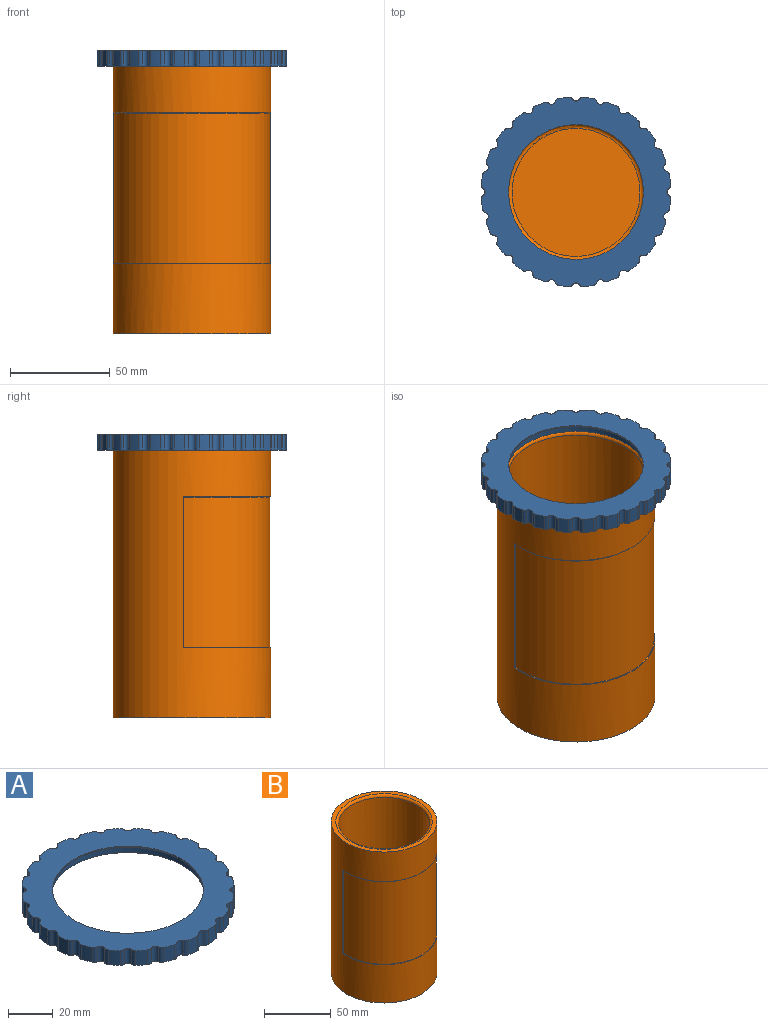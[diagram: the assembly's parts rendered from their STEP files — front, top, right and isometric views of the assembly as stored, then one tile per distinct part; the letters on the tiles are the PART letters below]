
ASSEMBLY  parts=2 mates=1
PART A: 103 faces, bbox 94.7x94.7x8 mm
  f0: cylinder r=34.5mm len=69mm, axis (0,0,-1), area 737mm2, adj f100,f102
  f1: cylinder r=47.5mm len=8mm, axis (0,0,-1), area 42.8mm2, adj f25,f26,f29,f97
  f2: cylinder r=47.5mm len=8mm, axis (0,0,-1), area 42.8mm2, adj f25,f26,f94,f98
  f3: cylinder r=47.5mm len=8mm, axis (0,0,-1), area 42.8mm2, adj f25,f26,f91,f95
  f4: cylinder r=47.5mm len=8mm, axis (0,0,-1), area 42.8mm2, adj f25,f26,f88,f92
  f5: cylinder r=47.5mm len=8mm, axis (0,0,-1), area 42.8mm2, adj f25,f26,f85,f89
  f6: cylinder r=47.5mm len=8mm, axis (0,0,-1), area 42.8mm2, adj f25,f26,f82,f86
  f7: cylinder r=47.5mm len=8mm, axis (0,0,-1), area 42.8mm2, adj f25,f26,f79,f83
  f8: cylinder r=47.5mm len=8mm, axis (0,0,-1), area 42.8mm2, adj f25,f26,f76,f80
  f9: cylinder r=47.5mm len=8mm, axis (0,0,-1), area 42.8mm2, adj f25,f26,f73,f77
  f10: cylinder r=47.5mm len=8mm, axis (0,0,-1), area 42.8mm2, adj f25,f26,f70,f74
  f11: cylinder r=47.5mm len=8mm, axis (0,0,-1), area 42.8mm2, adj f25,f26,f67,f71
  f12: cylinder r=47.5mm len=8mm, axis (0,0,-1), area 42.8mm2, adj f25,f26,f64,f68
  f13: cylinder r=47.5mm len=8mm, axis (0,0,-1), area 42.8mm2, adj f25,f26,f61,f65
  f14: cylinder r=47.5mm len=8mm, axis (0,0,-1), area 42.8mm2, adj f25,f26,f58,f62
  f15: cylinder r=47.5mm len=8mm, axis (0,0,-1), area 42.8mm2, adj f25,f26,f55,f59
  f16: cylinder r=47.5mm len=8mm, axis (0,0,-1), area 42.8mm2, adj f25,f26,f52,f56
  f17: cylinder r=47.5mm len=8mm, axis (0,0,-1), area 42.8mm2, adj f25,f26,f49,f53
  f18: cylinder r=47.5mm len=8mm, axis (0,0,-1), area 42.8mm2, adj f25,f26,f46,f50
  f19: cylinder r=47.5mm len=8mm, axis (0,0,-1), area 42.8mm2, adj f25,f26,f43,f47
  f20: cylinder r=47.5mm len=8mm, axis (0,0,-1), area 42.8mm2, adj f25,f26,f40,f44
  f21: cylinder r=47.5mm len=8mm, axis (0,0,-1), area 42.8mm2, adj f25,f26,f37,f41
  f22: cylinder r=47.5mm len=8mm, axis (0,0,-1), area 42.8mm2, adj f25,f26,f34,f38
  f23: cylinder r=47.5mm len=8mm, axis (0,0,-1), area 42.8mm2, adj f25,f26,f31,f35
  f24: cylinder r=47.5mm len=8mm, axis (0,0,-1), area 42.8mm2, adj f25,f26,f28,f32
  f25: plane 94.75x94.75mm, normal (0,0,1), area 3354mm2, adj f1,f2,f3,f4,f5,f6,f7,f8
  f26: plane 94.75x94.75mm, normal (0,0,-1), area 1895.3mm2, adj f1,f2,f3,f4,f5,f6,f7,f8
  f27: cylinder r=2mm len=8mm, axis (0,0,1), area 32.3mm2, adj f25,f26,f28,f29
  f28: cylinder r=2mm len=8mm, axis (0,0,-1), area 17.4mm2, adj f24,f25,f26,f27
  f29: cylinder r=2mm len=8mm, axis (0,0,-1), area 17.4mm2, adj f1,f25,f26,f27
  f30: cylinder r=2mm len=8mm, axis (0,0,1), area 32.3mm2, adj f25,f26,f31,f32
  f31: cylinder r=2mm len=8mm, axis (0,0,-1), area 17.4mm2, adj f23,f25,f26,f30
  f32: cylinder r=2mm len=8mm, axis (0,0,-1), area 17.4mm2, adj f24,f25,f26,f30
  f33: cylinder r=2mm len=8mm, axis (0,0,1), area 32.3mm2, adj f25,f26,f34,f35
  f34: cylinder r=2mm len=8mm, axis (0,0,-1), area 17.4mm2, adj f22,f25,f26,f33
  f35: cylinder r=2mm len=8mm, axis (0,0,-1), area 17.4mm2, adj f23,f25,f26,f33
  f36: cylinder r=2mm len=8mm, axis (0,0,1), area 32.3mm2, adj f25,f26,f37,f38
  f37: cylinder r=2mm len=8mm, axis (0,0,-1), area 17.4mm2, adj f21,f25,f26,f36
  f38: cylinder r=2mm len=8mm, axis (0,0,-1), area 17.4mm2, adj f22,f25,f26,f36
  f39: cylinder r=2mm len=8mm, axis (0,0,1), area 32.3mm2, adj f25,f26,f40,f41
  f40: cylinder r=2mm len=8mm, axis (0,0,-1), area 17.4mm2, adj f20,f25,f26,f39
  f41: cylinder r=2mm len=8mm, axis (0,0,-1), area 17.4mm2, adj f21,f25,f26,f39
  f42: cylinder r=2mm len=8mm, axis (0,0,1), area 32.3mm2, adj f25,f26,f43,f44
  f43: cylinder r=2mm len=8mm, axis (0,0,-1), area 17.4mm2, adj f19,f25,f26,f42
  f44: cylinder r=2mm len=8mm, axis (0,0,-1), area 17.4mm2, adj f20,f25,f26,f42
  f45: cylinder r=2mm len=8mm, axis (0,0,1), area 32.3mm2, adj f25,f26,f46,f47
  f46: cylinder r=2mm len=8mm, axis (0,0,-1), area 17.4mm2, adj f18,f25,f26,f45
  f47: cylinder r=2mm len=8mm, axis (0,0,-1), area 17.4mm2, adj f19,f25,f26,f45
  f48: cylinder r=2mm len=8mm, axis (0,0,1), area 32.3mm2, adj f25,f26,f49,f50
  f49: cylinder r=2mm len=8mm, axis (0,0,-1), area 17.4mm2, adj f17,f25,f26,f48
  f50: cylinder r=2mm len=8mm, axis (0,0,-1), area 17.4mm2, adj f18,f25,f26,f48
  f51: cylinder r=2mm len=8mm, axis (0,0,1), area 32.3mm2, adj f25,f26,f52,f53
  f52: cylinder r=2mm len=8mm, axis (0,0,-1), area 17.4mm2, adj f16,f25,f26,f51
  f53: cylinder r=2mm len=8mm, axis (0,0,-1), area 17.4mm2, adj f17,f25,f26,f51
  f54: cylinder r=2mm len=8mm, axis (0,0,1), area 32.3mm2, adj f25,f26,f55,f56
  f55: cylinder r=2mm len=8mm, axis (0,0,-1), area 17.4mm2, adj f15,f25,f26,f54
  f56: cylinder r=2mm len=8mm, axis (0,0,-1), area 17.4mm2, adj f16,f25,f26,f54
  f57: cylinder r=2mm len=8mm, axis (0,0,1), area 32.3mm2, adj f25,f26,f58,f59
  f58: cylinder r=2mm len=8mm, axis (0,0,-1), area 17.4mm2, adj f14,f25,f26,f57
  f59: cylinder r=2mm len=8mm, axis (0,0,-1), area 17.4mm2, adj f15,f25,f26,f57
  f60: cylinder r=2mm len=8mm, axis (0,0,1), area 32.3mm2, adj f25,f26,f61,f62
  f61: cylinder r=2mm len=8mm, axis (0,0,-1), area 17.4mm2, adj f13,f25,f26,f60
  f62: cylinder r=2mm len=8mm, axis (0,0,-1), area 17.4mm2, adj f14,f25,f26,f60
  f63: cylinder r=2mm len=8mm, axis (0,0,1), area 32.3mm2, adj f25,f26,f64,f65
  f64: cylinder r=2mm len=8mm, axis (0,0,-1), area 17.4mm2, adj f12,f25,f26,f63
  f65: cylinder r=2mm len=8mm, axis (0,0,-1), area 17.4mm2, adj f13,f25,f26,f63
  f66: cylinder r=2mm len=8mm, axis (0,0,1), area 32.3mm2, adj f25,f26,f67,f68
  f67: cylinder r=2mm len=8mm, axis (0,0,-1), area 17.4mm2, adj f11,f25,f26,f66
  f68: cylinder r=2mm len=8mm, axis (0,0,-1), area 17.4mm2, adj f12,f25,f26,f66
  f69: cylinder r=2mm len=8mm, axis (0,0,1), area 32.3mm2, adj f25,f26,f70,f71
  f70: cylinder r=2mm len=8mm, axis (0,0,-1), area 17.4mm2, adj f10,f25,f26,f69
  f71: cylinder r=2mm len=8mm, axis (0,0,-1), area 17.4mm2, adj f11,f25,f26,f69
  f72: cylinder r=2mm len=8mm, axis (0,0,1), area 32.3mm2, adj f25,f26,f73,f74
  f73: cylinder r=2mm len=8mm, axis (0,0,-1), area 17.4mm2, adj f9,f25,f26,f72
  f74: cylinder r=2mm len=8mm, axis (0,0,-1), area 17.4mm2, adj f10,f25,f26,f72
  f75: cylinder r=2mm len=8mm, axis (0,0,1), area 32.3mm2, adj f25,f26,f76,f77
  f76: cylinder r=2mm len=8mm, axis (0,0,-1), area 17.4mm2, adj f8,f25,f26,f75
  f77: cylinder r=2mm len=8mm, axis (0,0,-1), area 17.4mm2, adj f9,f25,f26,f75
  f78: cylinder r=2mm len=8mm, axis (0,0,1), area 32.3mm2, adj f25,f26,f79,f80
  f79: cylinder r=2mm len=8mm, axis (0,0,-1), area 17.4mm2, adj f7,f25,f26,f78
  f80: cylinder r=2mm len=8mm, axis (0,0,-1), area 17.4mm2, adj f8,f25,f26,f78
  f81: cylinder r=2mm len=8mm, axis (0,0,1), area 32.3mm2, adj f25,f26,f82,f83
  f82: cylinder r=2mm len=8mm, axis (0,0,-1), area 17.4mm2, adj f6,f25,f26,f81
  f83: cylinder r=2mm len=8mm, axis (0,0,-1), area 17.4mm2, adj f7,f25,f26,f81
  f84: cylinder r=2mm len=8mm, axis (0,0,1), area 32.3mm2, adj f25,f26,f85,f86
  f85: cylinder r=2mm len=8mm, axis (0,0,-1), area 17.4mm2, adj f5,f25,f26,f84
  f86: cylinder r=2mm len=8mm, axis (0,0,-1), area 17.4mm2, adj f6,f25,f26,f84
  f87: cylinder r=2mm len=8mm, axis (0,0,1), area 32.3mm2, adj f25,f26,f88,f89
  f88: cylinder r=2mm len=8mm, axis (0,0,-1), area 17.4mm2, adj f4,f25,f26,f87
  f89: cylinder r=2mm len=8mm, axis (0,0,-1), area 17.4mm2, adj f5,f25,f26,f87
  f90: cylinder r=2mm len=8mm, axis (0,0,1), area 32.3mm2, adj f25,f26,f91,f92
  f91: cylinder r=2mm len=8mm, axis (0,0,-1), area 17.4mm2, adj f3,f25,f26,f90
  f92: cylinder r=2mm len=8mm, axis (0,0,-1), area 17.4mm2, adj f4,f25,f26,f90
  f93: cylinder r=2mm len=8mm, axis (0,0,1), area 32.3mm2, adj f25,f26,f94,f95
  f94: cylinder r=2mm len=8mm, axis (0,0,-1), area 17.4mm2, adj f2,f25,f26,f93
  f95: cylinder r=2mm len=8mm, axis (0,0,-1), area 17.4mm2, adj f3,f25,f26,f93
  f96: cylinder r=2mm len=8mm, axis (0,0,1), area 32.3mm2, adj f25,f26,f97,f98
  f97: cylinder r=2mm len=8mm, axis (0,0,-1), area 17.4mm2, adj f1,f25,f26,f96
  f98: cylinder r=2mm len=8mm, axis (0,0,-1), area 17.4mm2, adj f2,f25,f26,f96
  f99: cylinder r=40mm len=80mm, axis (0,0,-1), area 1005.3mm2, adj f26,f100
  f100: plane 80x80mm, normal (0,0,-1), area 1287.3mm2, adj f0,f99
  f101: cylinder r=33.7mm len=67.4mm, axis (0,0,1), area 127mm2, adj f25,f102
  f102: plane 69x69mm, normal (0,0,-1), area 171.4mm2, adj f0,f101
PART B: 12 faces, bbox 86.4x82.7x138 mm
  f0: cylinder r=39.5mm len=138mm, axis (0,0,-1), area 24137.4mm2, adj f1,f2,f6,f7,f8,f9
  f1: plane 79x79mm, normal (0,0,1), area 830.2mm2, adj f0,f10
  f2: plane 79x79mm, normal (0,0,-1), area 4901.7mm2, adj f0
  f3: cylinder r=34mm len=126mm, axis (0,0,1), area 26917.2mm2, adj f10,f11
  f4: plane 64x64mm, normal (0,0,1), area 3217mm2, adj f11
  f5: cylinder r=38.9mm len=77.8mm, axis (0,0,1), area 9880mm2, adj f6,f7,f8,f9
  f6: plane 76x0.6mm, normal (-0.11,-0.99,0), area 45.5mm2, adj f0,f5,f8,f9
  f7: plane 76x0.6mm, normal (0.11,-0.99,0), area 45.5mm2, adj f0,f5,f8,f9
  f8: plane 79x43.97mm, normal (0,0,1), area 79.2mm2, adj f0,f5,f6,f7
  f9: torus R=39.5mm, axis (0,0,1), area 124.2mm2, adj f0,f5,f6,f7
  f10: torus R=36mm, axis (0,0,1), area 685.5mm2, adj f1,f3
  f11: torus R=32mm, axis (0,0,-1), area 656.8mm2, adj f3,f4
PLACE A t=(0,0,134)mm
PLACE B at identity
MATE revolute A.f0 <-> B.f0  axis (0,0,-1) through (0,0,138)mm
